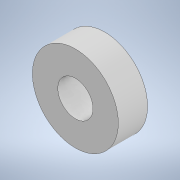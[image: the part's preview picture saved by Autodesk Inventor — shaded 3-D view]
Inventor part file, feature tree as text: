
AUTODESK INVENTOR PART (.ipt)
format: ipt  version: 2021 (Build 250183000, 183)  size: 96,256 bytes
history: native  units: mm
features: extrude x1, sketch x1
ambient origin geometry x8: Origin, YZ Plane, XZ Plane, XY Plane, X Axis, Y Axis, Z Axis, Center Point
bodies: Solid1 (feature_tree)
feature tree (2):
  extrude  "Extrusion1"  Depth=7.5mm
  sketch  "Sketch1"  dims[d0=9.0mm d1=22.0mm d2=7.5mm d3=0.0mm]
